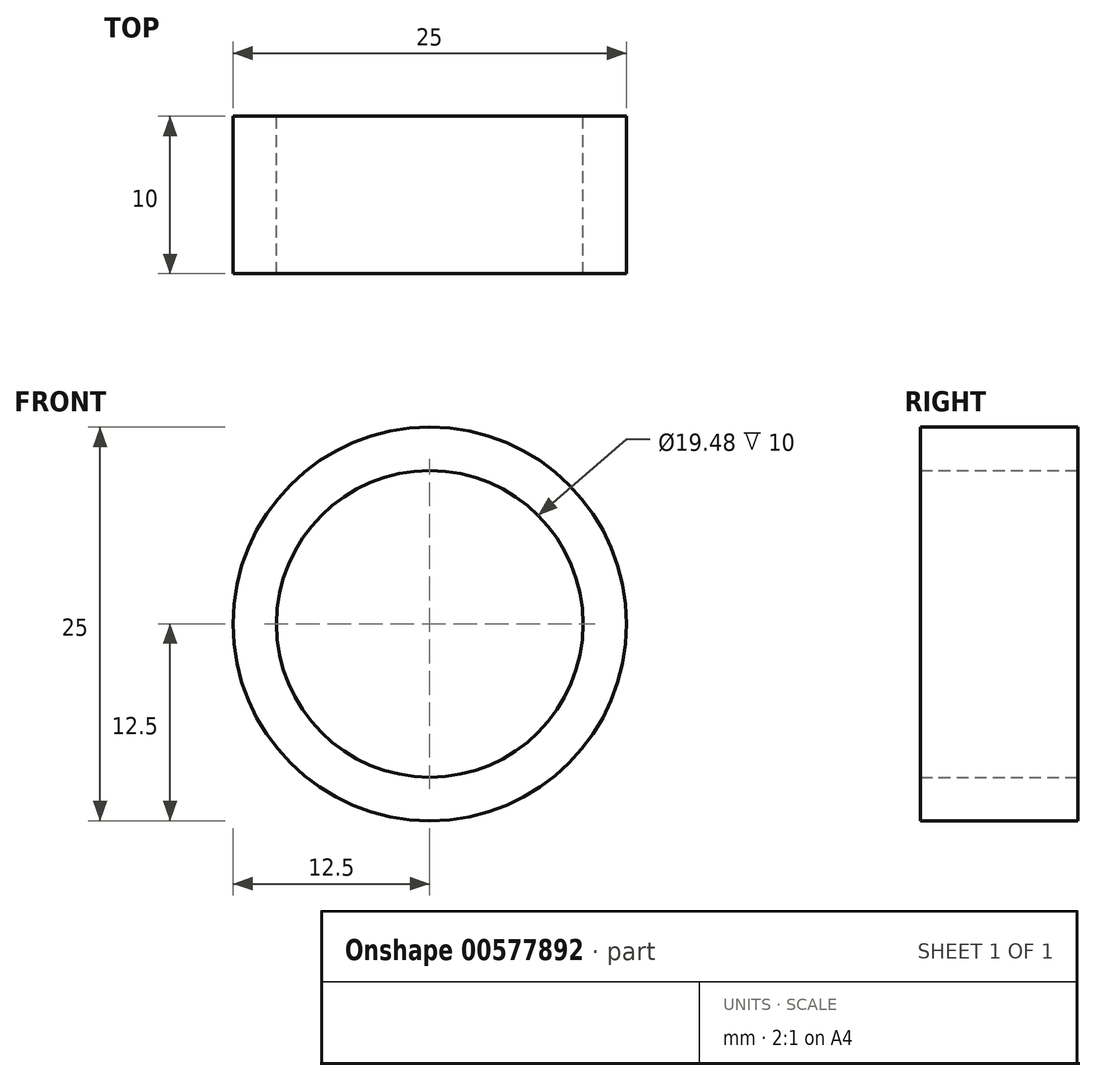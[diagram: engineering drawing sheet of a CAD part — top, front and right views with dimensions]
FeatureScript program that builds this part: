
annotation { "Feature Type Name" : "Feature", "Feature Type Description" : "" }
export const myFeature = defineFeature(function(context is Context, id is Id, definition is map)
    precondition{}
    {
        {
            var Q0;
            Q0=qCreatedBy(makeId("Front.planeOp"),FACE);
            var sketch = newSketch(context, id + "F0", { "sketchPlane" : qUnion([Q0])});
            skCircle(sketch, "E0", {"center": v(0, 0) * mm, "radius": 12.5 * mm});
            skCircle(sketch, "E1", {"center": v(0, 0) * mm, "radius": 9.74 * mm});
            skSolve(sketch);
        }
        {
            var Q0;
            Q0=makeQuery(id+"F0.imprint","IMPRINT",FACE,{"disambiguationData":[TD([[makeQuery(id+"F0.imprint","IMPRINT",EDGE,{"derivedFrom":sQuery(id+"F0.wireOp",EDGE,"E0")}),1.0]])]});
            extrude(context, id + "F1", {"entities" : qUnion([Q0]), "depth" : 10 * mm, "offsetDistance" : 25 * mm});
        }
    });
